# Revit family: BRG-SNT-INS_TAZA SULTÁN HET BLANCO-ORQUÁDEA SIN TAPA
name_source: partatom
category: Aparatos sanitarios
units: mm (PartAtom-declared; Revit-internal decimal feet)

## family parameters
Compartido = Sí
Corte con vacíos al cargar = No
Cota de conector redondo = Diámetro de uso
Número OmniClass = 23.45.00.00
Punto de cálculo de habitación = Sí
Se basa en plano de trabajo = No
Siempre vertical = Sí
Tipo de pieza = Normal
Título OmniClass = Sanitary, Laundry, and Cleaning Equipment

## types (1)
- TAZA SULTAN HET SIN CARRIER
    Conexión AC = Sí
    Conexión AF = Sí
    Conexión de residuos = Sí
    Conexión de ventilación = Sí
    Fabricante = BRIGGS Ecuador
    Imagen de tipo = <Ninguno>
    Modelo = TAZA SULTAN HET SIN CARRIER
    URL = https://www.briggs.com.ec
    _ALT_Basamento = 0.4 m
    _ALT_Eje instalación = 0.6 m
    _EDESA_ Alto en cm = 39
    _EDESA_ Ancho en cm = 35.8
    _EDESA_ Categoría = Productos > Sanitarios > Institucional
    _EDESA_ Certificación = Cumple con norma NTE INEN 3082
    _EDESA_ Color = blanco
    _EDESA_ Consumo/capacidad de agua en L = 4.8 litros
    _EDESA_ Cumple normativa ADA = Si cumple
    _EDESA_ Descripción = Taza de inodoro suspendida en la pared con asiento de caída libre. Funciona con fluxómetro o llave temporizada.
    _EDESA_ Distancia de instalación en cm (muro terminado) = 0
    _EDESA_ Garantía = De por vida en funcionamiento y acabado de la cerámica sanitaria
    _EDESA_ Manual de instalación = https://www.briggs.com.ec
    _EDESA_ Marca = BRIGGS
    _EDESA_ Materiales = Cerámica Sanitaria
    _EDESA_ Nombre = TAZA SULTAN HET SIN CARRIER
    _EDESA_ Peso en kg = 21.4 kg
    _EDESA_ Productos incluídos = Asiento Orquídea con tapa, Gasket, Spud de 1 1/2” para Taza, Tapas de Anclaje
    _EDESA_ Productos necesarios para instalación = Fluxómetro, Carrier de soporte
    _EDESA_ Profundidad en cm = 63.7
    _EDESA_ Sku/código = JS0077801301CB
    _EDESA_ Tipo de Aro = 0
    _EDESA_ Tipo de instalación = Anclado al muro (fijar con carrier)
